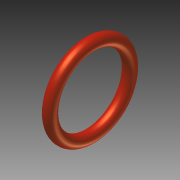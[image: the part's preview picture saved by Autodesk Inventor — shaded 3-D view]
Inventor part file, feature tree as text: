
AUTODESK INVENTOR PART (.ipt)
format: ipt  version: 2012 SP1 (Build 160190100, 190)  size: 114,688 bytes
history: native  units: in
note: dims shown in document units (in); Inventor stores cm internally (conversion verified against a paired STEP export)
features: sketch x2, sweep x1
ambient origin geometry x8: Origin, YZ Plane, XZ Plane, XY Plane, X Axis, Y Axis, Z Axis, Center Point
bodies: Solid1 (feature_tree)
feature tree (3):
  sweep  "Sweep1"
  sketch  "Sketch1"  dims[d0=0.103in d1=0.612in]
  sketch  "Sketch2"  dims[d2=0.0in]
